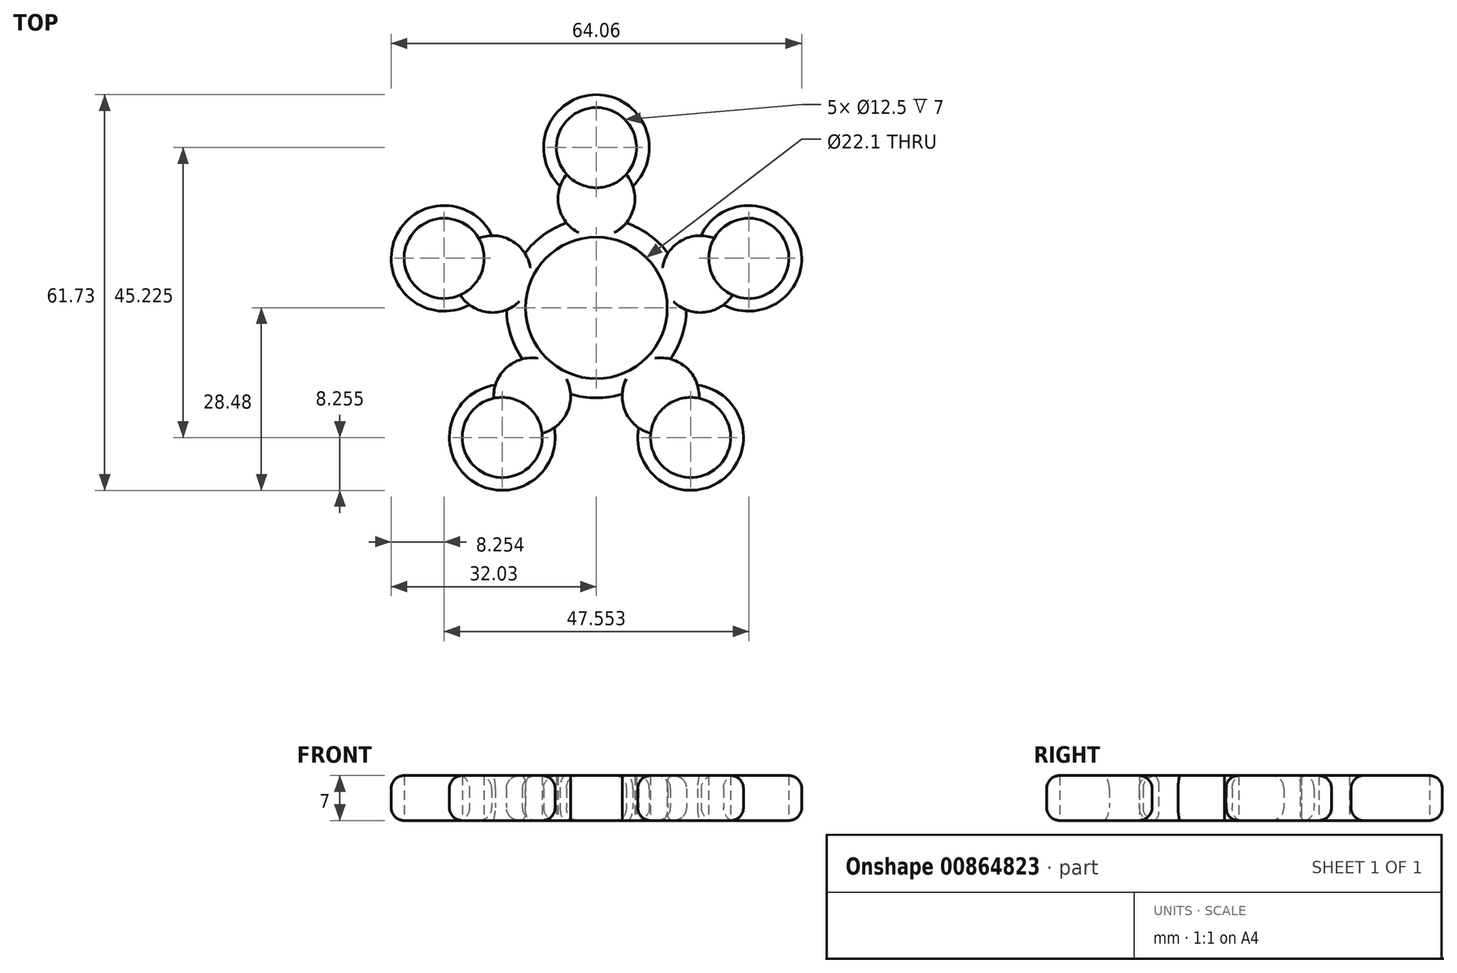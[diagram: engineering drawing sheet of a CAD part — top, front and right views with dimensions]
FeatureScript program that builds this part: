
annotation { "Feature Type Name" : "Feature", "Feature Type Description" : "" }
export const myFeature = defineFeature(function(context is Context, id is Id, definition is map)
    precondition{}
    {
        {
            var Q0;
            Q0=qCreatedBy(makeId("Top.planeOp"),FACE);
            var sketch = newSketch(context, id + "F0", { "sketchPlane" : qUnion([Q0])});
            skCircle(sketch, "E0", {"center": v(0, 0) * mm, "radius": 11.05 * mm});
            skArc(sketch, "E1.0", {"start": v(-4.65, 13.26) * mm, "mid": v(0, -14.05) * mm, "end": v(4.65, 13.26) * mm});
            skCircle(sketch, "E2", {"center": v(0, 25) * mm, "radius": 6.25 * mm});
            skArc(sketch, "E3.0", {"start": v(5.67, 19) * mm, "mid": v(0, 33.25) * mm, "end": v(-5.67, 19) * mm});
            skArc(sketch, "E4", {"start": v(-5.67, 19) * mm, "mid": v(-5.9, 16) * mm, "end": v(-4.65, 13.26) * mm});
            skArc(sketch, "E5.trimOffspring", {"start": v(4.65, 13.26) * mm, "mid": v(5.9, 16) * mm, "end": v(5.67, 19) * mm});
            skLineSegment(sketch, "E6", {"start": v(0, 44.58) * mm, "end": v(0, 18.67) * mm});
            skArc(sketch, "E7", {"start": v(0, 31.25) * mm, "mid": v(6.25, 25) * mm, "end": v(0, 18.75) * mm});
            skSolve(sketch);
        }
        {
            var Q0;
            Q0 = qSketchRegion(id + "F0", true);
            extrude(context, id + "F1", {"entities" : qUnion([Q0]), "endBound" : BoundingType.SYMMETRIC, "depth" : 7 * mm, "offsetDistance" : 25 * mm});
        }
        {
            var Q0;
            Q0=sQuery(id+"F0.wireOp",EDGE,"E7");
            var Q1;
            Q1=sQuery(id+"F0.wireOp",EDGE,"E6");
            revolve(context, id + "F2", {"bodyType" : ToolBodyType.SURFACE, "surfaceOperationType" : NewSurfaceOperationType.NEW, "surfaceEntities" : qUnion([Q0]), "axis" : qUnion([Q1]), "revolveType" : RevolveType.FULL});
        }
        {
            var Q0;
            Q0=makeQuery(id+"F1.opExtrude","SWEPT_BODY",BODY,{"disambiguationData":[OSD([sQuery(id+"F0.wireOp",EDGE,"E0"),sQuery(id+"F0.wireOp",EDGE,"E1.0"),sQuery(id+"F0.wireOp",EDGE,"E2"),sQuery(id+"F0.wireOp",EDGE,"E3.0"),sQuery(id+"F0.wireOp",EDGE,"E4"),sQuery(id+"F0.wireOp",EDGE,"E5.trimOffspring")])]});
            var Q1;
            Q1=makeQuery(id+"F1.opExtrude","CAP_EDGE",EDGE,{"disambiguationData":[OSD([sQuery(id+"F0.wireOp",EDGE,"E0")])],"isStart":false});
            circularPattern(context, id + "F3", {"entities" : qUnion([Q0]), "axis" : qUnion([Q1]), "angle" : 360 * degree, "instanceCount" : 5, "equalSpace" : true});
        }
        {
            var Q0;
            Q0=makeQuery(id+"F3.opPattern","COPY",BODY,{"derivedFrom":makeQuery(id+"F1.opExtrude","SWEPT_BODY",BODY,{"disambiguationData":[OSD([sQuery(id+"F0.wireOp",EDGE,"E0"),sQuery(id+"F0.wireOp",EDGE,"E1.0"),sQuery(id+"F0.wireOp",EDGE,"E2"),sQuery(id+"F0.wireOp",EDGE,"E3.0"),sQuery(id+"F0.wireOp",EDGE,"E4"),sQuery(id+"F0.wireOp",EDGE,"E5.trimOffspring")])]}),"instanceName":"4"});
            var Q1;
            Q1=makeQuery(id+"F3.opPattern","COPY",BODY,{"derivedFrom":makeQuery(id+"F1.opExtrude","SWEPT_BODY",BODY,{"disambiguationData":[OSD([sQuery(id+"F0.wireOp",EDGE,"E0"),sQuery(id+"F0.wireOp",EDGE,"E1.0"),sQuery(id+"F0.wireOp",EDGE,"E2"),sQuery(id+"F0.wireOp",EDGE,"E3.0"),sQuery(id+"F0.wireOp",EDGE,"E4"),sQuery(id+"F0.wireOp",EDGE,"E5.trimOffspring")])]}),"instanceName":"3"});
            var Q2;
            Q2=makeQuery(id+"F3.opPattern","COPY",BODY,{"derivedFrom":makeQuery(id+"F1.opExtrude","SWEPT_BODY",BODY,{"disambiguationData":[OSD([sQuery(id+"F0.wireOp",EDGE,"E0"),sQuery(id+"F0.wireOp",EDGE,"E1.0"),sQuery(id+"F0.wireOp",EDGE,"E2"),sQuery(id+"F0.wireOp",EDGE,"E3.0"),sQuery(id+"F0.wireOp",EDGE,"E4"),sQuery(id+"F0.wireOp",EDGE,"E5.trimOffspring")])]}),"instanceName":"1"});
            var Q3;
            Q3=makeQuery(id+"F3.opPattern","COPY",BODY,{"derivedFrom":makeQuery(id+"F1.opExtrude","SWEPT_BODY",BODY,{"disambiguationData":[OSD([sQuery(id+"F0.wireOp",EDGE,"E0"),sQuery(id+"F0.wireOp",EDGE,"E1.0"),sQuery(id+"F0.wireOp",EDGE,"E2"),sQuery(id+"F0.wireOp",EDGE,"E3.0"),sQuery(id+"F0.wireOp",EDGE,"E4"),sQuery(id+"F0.wireOp",EDGE,"E5.trimOffspring")])]}),"instanceName":"2"});
            var Q4;
            Q4=makeQuery(id+"F1.opExtrude","SWEPT_BODY",BODY,{"disambiguationData":[OSD([sQuery(id+"F0.wireOp",EDGE,"E0"),sQuery(id+"F0.wireOp",EDGE,"E1.0"),sQuery(id+"F0.wireOp",EDGE,"E2"),sQuery(id+"F0.wireOp",EDGE,"E3.0"),sQuery(id+"F0.wireOp",EDGE,"E4"),sQuery(id+"F0.wireOp",EDGE,"E5.trimOffspring")])]});
            booleanBodies(context, id + "F4", {"operationType" : BooleanOperationType.UNION, "tools" : qUnion([Q0, Q1, Q2, Q3, Q4])});
        }
        {
            var Q0;
            Q0=makeQuery(id+"F3.opPattern","COPY",EDGE,{"derivedFrom":makeQuery(id+"F1.opExtrude","CAP_EDGE",EDGE,{"disambiguationData":[OSD([sQuery(id+"F0.wireOp",EDGE,"E0")])],"isStart":false}),"instanceName":"4"});
            var Q1;
            Q1=makeQuery(id+"F3.opPattern","COPY",EDGE,{"derivedFrom":makeQuery(id+"F1.opExtrude","CAP_EDGE",EDGE,{"disambiguationData":[OSD([sQuery(id+"F0.wireOp",EDGE,"E0")])],"isStart":true}),"instanceName":"4"});
            fillet(context, id + "F5", {"entities" : qUnion([Q0, Q1]), "radius" : 1 * mm, "tangentPropagation" : true, "allowEdgeOverflow" : false});
        }
        {
            var Q0;
            Q0=makeQuery(id+"F1.opExtrude","CAP_EDGE",EDGE,{"disambiguationData":[OSD([sQuery(id+"F0.wireOp",EDGE,"E3.0")])],"isStart":false});
            var Q1;
            Q1=makeQuery(id+"F3.opPattern","COPY",EDGE,{"derivedFrom":makeQuery(id+"F1.opExtrude","CAP_EDGE",EDGE,{"disambiguationData":[OSD([sQuery(id+"F0.wireOp",EDGE,"E3.0")])],"isStart":false}),"instanceName":"4"});
            var Q2;
            Q2=makeQuery(id+"F3.opPattern","COPY",EDGE,{"derivedFrom":makeQuery(id+"F1.opExtrude","CAP_EDGE",EDGE,{"disambiguationData":[OSD([sQuery(id+"F0.wireOp",EDGE,"E3.0")])],"isStart":false}),"instanceName":"3"});
            var Q3;
            Q3=makeQuery(id+"F3.opPattern","COPY",EDGE,{"derivedFrom":makeQuery(id+"F1.opExtrude","CAP_EDGE",EDGE,{"disambiguationData":[OSD([sQuery(id+"F0.wireOp",EDGE,"E3.0")])],"isStart":false}),"instanceName":"2"});
            var Q4;
            Q4=makeQuery(id+"F3.opPattern","COPY",EDGE,{"derivedFrom":makeQuery(id+"F1.opExtrude","CAP_EDGE",EDGE,{"disambiguationData":[OSD([sQuery(id+"F0.wireOp",EDGE,"E3.0")])],"isStart":false}),"instanceName":"1"});
            var Q5;
            {var subQ1=sQuery(id+"F0.wireOp",EDGE,"E4");var subQ2=sQuery(id+"F0.wireOp",EDGE,"E1.0");Q5=makeQuery(id+"F4.opBoolean","SPLIT",EDGE,{"disambiguationData":[TD([makeQuery(id+"F1.opExtrude","SWEPT_FACE",FACE,{"disambiguationData":[OSD([subQ1])]})])],"derivedFrom":makeQuery(id+"F3.opPattern","COPY",EDGE,{"derivedFrom":makeQuery(id+"F1.opExtrude","CAP_EDGE",EDGE,{"disambiguationData":[OSD([subQ2])],"isStart":false}),"instanceName":"4"})});}
            var Q6;
            {var subQ0=sQuery(id+"F0.wireOp",EDGE,"E5.trimOffspring");var subQ2=sQuery(id+"F0.wireOp",EDGE,"E1.0");Q6=makeQuery(id+"F4.opBoolean","SPLIT",EDGE,{"disambiguationData":[TD([makeQuery(id+"F1.opExtrude","SWEPT_FACE",FACE,{"disambiguationData":[OSD([subQ0])]})])],"derivedFrom":makeQuery(id+"F3.opPattern","COPY",EDGE,{"derivedFrom":makeQuery(id+"F1.opExtrude","CAP_EDGE",EDGE,{"disambiguationData":[OSD([subQ2])],"isStart":false}),"instanceName":"4"})});}
            var Q7;
            {var subQ1=sQuery(id+"F0.wireOp",EDGE,"E4");var subQ2=sQuery(id+"F0.wireOp",EDGE,"E1.0");Q7=makeQuery(id+"F4.opBoolean","SPLIT",EDGE,{"disambiguationData":[TD([makeQuery(id+"F3.opPattern","COPY",FACE,{"derivedFrom":makeQuery(id+"F1.opExtrude","SWEPT_FACE",FACE,{"disambiguationData":[OSD([subQ1])]}),"instanceName":"3"})])],"derivedFrom":makeQuery(id+"F3.opPattern","COPY",EDGE,{"derivedFrom":makeQuery(id+"F1.opExtrude","CAP_EDGE",EDGE,{"disambiguationData":[OSD([subQ2])],"isStart":false}),"instanceName":"4"})});}
            var Q8;
            {var subQ0=sQuery(id+"F0.wireOp",EDGE,"E4");var subQ2=sQuery(id+"F0.wireOp",EDGE,"E1.0");Q8=makeQuery(id+"F4.opBoolean","SPLIT",EDGE,{"disambiguationData":[TD([makeQuery(id+"F3.opPattern","COPY",FACE,{"derivedFrom":makeQuery(id+"F1.opExtrude","SWEPT_FACE",FACE,{"disambiguationData":[OSD([subQ0])]}),"instanceName":"2"})])],"derivedFrom":makeQuery(id+"F3.opPattern","COPY",EDGE,{"derivedFrom":makeQuery(id+"F1.opExtrude","CAP_EDGE",EDGE,{"disambiguationData":[OSD([subQ2])],"isStart":false}),"instanceName":"4"})});}
            var Q9;
            {var subQ0=sQuery(id+"F0.wireOp",EDGE,"E4");var subQ2=sQuery(id+"F0.wireOp",EDGE,"E1.0");Q9=makeQuery(id+"F4.opBoolean","SPLIT",EDGE,{"disambiguationData":[TD([makeQuery(id+"F3.opPattern","COPY",FACE,{"derivedFrom":makeQuery(id+"F1.opExtrude","SWEPT_FACE",FACE,{"disambiguationData":[OSD([subQ0])]}),"instanceName":"1"})])],"derivedFrom":makeQuery(id+"F3.opPattern","COPY",EDGE,{"derivedFrom":makeQuery(id+"F1.opExtrude","CAP_EDGE",EDGE,{"disambiguationData":[OSD([subQ2])],"isStart":false}),"instanceName":"4"})});}
            var Q10;
            Q10=makeQuery(id+"F3.opPattern","COPY",EDGE,{"derivedFrom":makeQuery(id+"F1.opExtrude","CAP_EDGE",EDGE,{"disambiguationData":[OSD([sQuery(id+"F0.wireOp",EDGE,"E3.0")])],"isStart":true}),"instanceName":"2"});
            var Q11;
            Q11=makeQuery(id+"F3.opPattern","COPY",EDGE,{"derivedFrom":makeQuery(id+"F1.opExtrude","CAP_EDGE",EDGE,{"disambiguationData":[OSD([sQuery(id+"F0.wireOp",EDGE,"E3.0")])],"isStart":true}),"instanceName":"3"});
            var Q12;
            Q12=makeQuery(id+"F3.opPattern","COPY",EDGE,{"derivedFrom":makeQuery(id+"F1.opExtrude","CAP_EDGE",EDGE,{"disambiguationData":[OSD([sQuery(id+"F0.wireOp",EDGE,"E3.0")])],"isStart":true}),"instanceName":"4"});
            var Q13;
            Q13=makeQuery(id+"F1.opExtrude","CAP_EDGE",EDGE,{"disambiguationData":[OSD([sQuery(id+"F0.wireOp",EDGE,"E3.0")])],"isStart":true});
            var Q14;
            Q14=makeQuery(id+"F3.opPattern","COPY",EDGE,{"derivedFrom":makeQuery(id+"F1.opExtrude","CAP_EDGE",EDGE,{"disambiguationData":[OSD([sQuery(id+"F0.wireOp",EDGE,"E3.0")])],"isStart":true}),"instanceName":"1"});
            var Q15;
            {var subQ0=sQuery(id+"F0.wireOp",EDGE,"E4");var subQ2=sQuery(id+"F0.wireOp",EDGE,"E1.0");Q15=makeQuery(id+"F4.opBoolean","SPLIT",EDGE,{"disambiguationData":[TD([makeQuery(id+"F3.opPattern","COPY",FACE,{"derivedFrom":makeQuery(id+"F1.opExtrude","SWEPT_FACE",FACE,{"disambiguationData":[OSD([subQ0])]}),"instanceName":"1"})])],"derivedFrom":makeQuery(id+"F3.opPattern","COPY",EDGE,{"derivedFrom":makeQuery(id+"F1.opExtrude","CAP_EDGE",EDGE,{"disambiguationData":[OSD([subQ2])],"isStart":true}),"instanceName":"4"})});}
            var Q16;
            {var subQ1=sQuery(id+"F0.wireOp",EDGE,"E4");var subQ2=sQuery(id+"F0.wireOp",EDGE,"E1.0");Q16=makeQuery(id+"F4.opBoolean","SPLIT",EDGE,{"disambiguationData":[TD([makeQuery(id+"F3.opPattern","COPY",FACE,{"derivedFrom":makeQuery(id+"F1.opExtrude","SWEPT_FACE",FACE,{"disambiguationData":[OSD([subQ1])]}),"instanceName":"2"})])],"derivedFrom":makeQuery(id+"F3.opPattern","COPY",EDGE,{"derivedFrom":makeQuery(id+"F1.opExtrude","CAP_EDGE",EDGE,{"disambiguationData":[OSD([subQ2])],"isStart":true}),"instanceName":"4"})});}
            var Q17;
            {var subQ1=sQuery(id+"F0.wireOp",EDGE,"E4");var subQ2=sQuery(id+"F0.wireOp",EDGE,"E1.0");Q17=makeQuery(id+"F4.opBoolean","SPLIT",EDGE,{"disambiguationData":[TD([makeQuery(id+"F3.opPattern","COPY",FACE,{"derivedFrom":makeQuery(id+"F1.opExtrude","SWEPT_FACE",FACE,{"disambiguationData":[OSD([subQ1])]}),"instanceName":"3"})])],"derivedFrom":makeQuery(id+"F3.opPattern","COPY",EDGE,{"derivedFrom":makeQuery(id+"F1.opExtrude","CAP_EDGE",EDGE,{"disambiguationData":[OSD([subQ2])],"isStart":true}),"instanceName":"4"})});}
            var Q18;
            {var subQ0=sQuery(id+"F0.wireOp",EDGE,"E5.trimOffspring");var subQ2=sQuery(id+"F0.wireOp",EDGE,"E1.0");Q18=makeQuery(id+"F4.opBoolean","SPLIT",EDGE,{"disambiguationData":[TD([makeQuery(id+"F1.opExtrude","SWEPT_FACE",FACE,{"disambiguationData":[OSD([subQ0])]})])],"derivedFrom":makeQuery(id+"F3.opPattern","COPY",EDGE,{"derivedFrom":makeQuery(id+"F1.opExtrude","CAP_EDGE",EDGE,{"disambiguationData":[OSD([subQ2])],"isStart":true}),"instanceName":"4"})});}
            var Q19;
            {var subQ1=sQuery(id+"F0.wireOp",EDGE,"E4");var subQ2=sQuery(id+"F0.wireOp",EDGE,"E1.0");Q19=makeQuery(id+"F4.opBoolean","SPLIT",EDGE,{"disambiguationData":[TD([makeQuery(id+"F1.opExtrude","SWEPT_FACE",FACE,{"disambiguationData":[OSD([subQ1])]})])],"derivedFrom":makeQuery(id+"F3.opPattern","COPY",EDGE,{"derivedFrom":makeQuery(id+"F1.opExtrude","CAP_EDGE",EDGE,{"disambiguationData":[OSD([subQ2])],"isStart":true}),"instanceName":"4"})});}
            fillet(context, id + "F6", {"entities" : qUnion([Q0, Q1, Q2, Q3, Q4, Q5, Q6, Q7, Q8, Q9, Q10, Q11, Q12, Q13, Q14, Q15, Q16, Q17, Q18, Q19]), "radius" : 2 * mm, "tangentPropagation" : true, "allowEdgeOverflow" : false});
        }
    });
